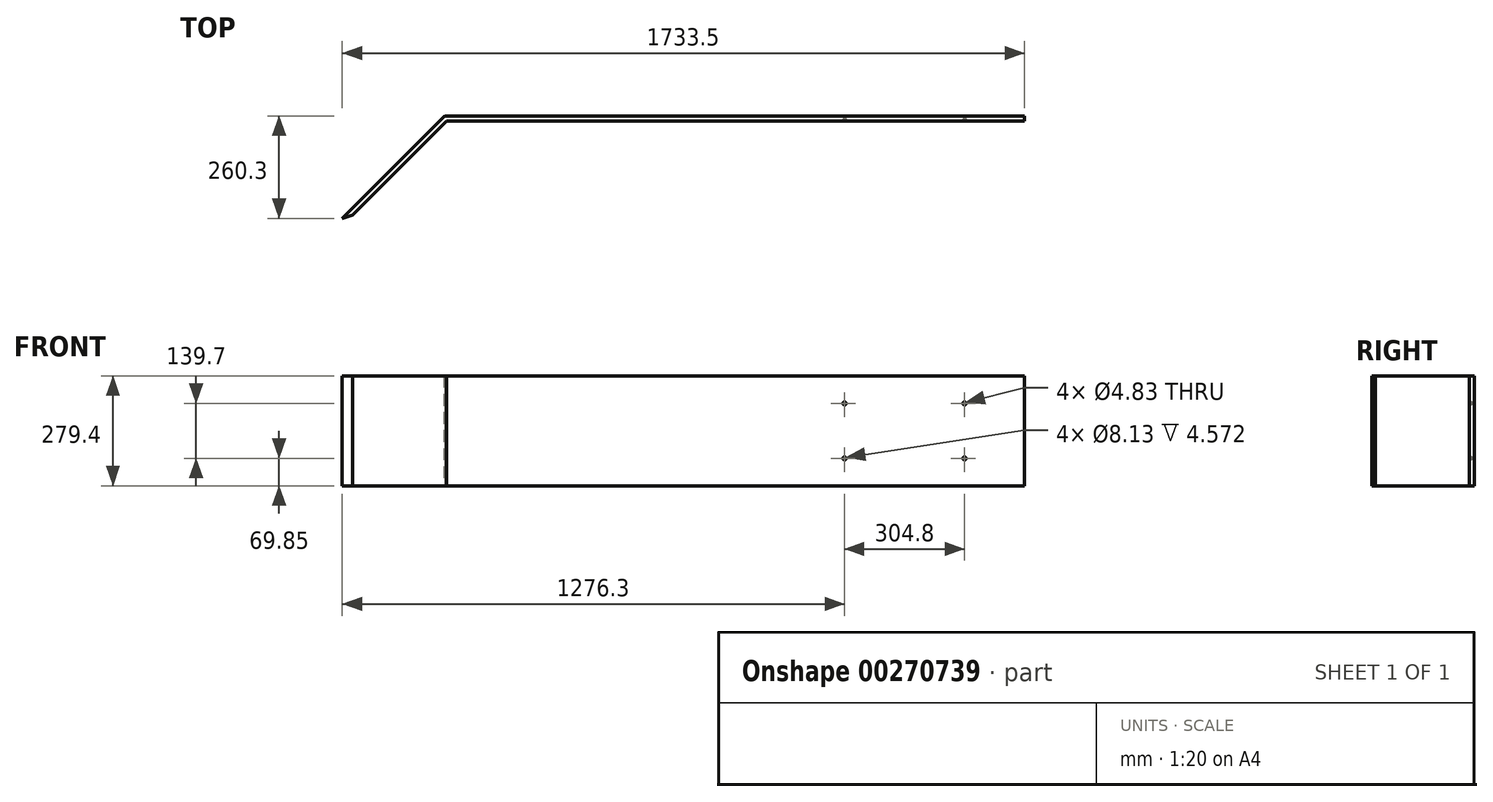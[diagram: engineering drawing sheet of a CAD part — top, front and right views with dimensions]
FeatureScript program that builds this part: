
annotation { "Feature Type Name" : "Feature", "Feature Type Description" : "" }
export const myFeature = defineFeature(function(context is Context, id is Id, definition is map)
    precondition{}
    {
        {
            var Q0;
            Q0=qCreatedBy(makeId("Front.planeOp"),FACE);
            var sketch = newSketch(context, id + "F0", { "sketchPlane" : qUnion([Q0])});
            skLineSegment(sketch, "E0.bottom", {"start": v(736.6, 139.7) * mm, "end": v(-736.6, 139.7) * mm});
            skLineSegment(sketch, "E0.top", {"start": v(736.6, -139.7) * mm, "end": v(-736.6, -139.7) * mm});
            skLineSegment(sketch, "E0.left", {"start": v(736.6, 139.7) * mm, "end": v(736.6, -139.7) * mm});
            skLineSegment(sketch, "E0.right", {"start": v(-736.6, 139.7) * mm, "end": v(-736.6, -139.7) * mm});
            skPoint(sketch, "E0.middle", {"position": v(0, 0) * mm});
            skSolve(sketch);
        }
        {
            var Q0;
            Q0 = qSketchRegion(id + "F0", true);
            extrude(context, id + "F1", {"entities" : qUnion([Q0]), "depth" : 12.7 * mm});
        }
        {
            var Q0;
            Q0=makeQuery(id+"F1.opExtrude","SWEPT_FACE",FACE,{"disambiguationData":[OSD([sQuery(id+"F0.wireOp",EDGE,"E0.bottom")])]});
            var sketch = newSketch(context, id + "F2", { "sketchPlane" : qUnion([Q0])});
            skLineSegment(sketch, "E1", {"start": v(-736.6, -12.7) * mm, "end": v(-736.6, 0) * mm});
            skLineSegment(sketch, "E2", {"start": v(-736.6, -12.7) * mm, "end": v(-731.34, -12.7) * mm});
            skLineSegment(sketch, "E3", {"start": v(-996.9, -260.3) * mm, "end": v(-736.6, 0) * mm});
            skLineSegment(sketch, "E4", {"start": v(-731.34, -12.7) * mm, "end": v(-969.96, -251.32) * mm});
            skLineSegment(sketch, "E5", {"start": v(-969.96, -251.32) * mm, "end": v(-996.9, -260.3) * mm});
            skSolve(sketch);
        }
        {
            var Q0;
            Q0 = qSketchRegion(id + "F2", true);
            extrude(context, id + "F3", {"entities" : qUnion([Q0]), "operationType" : NewBodyOperationType.ADD, "oppositeDirection" : true, "depth" : 279.4 * mm});
        }
        {
            var Q0;
            Q0=makeQuery(id+"F3.boolean.opBoolean","MERGE",EDGE,{"derivedFrom":[makeQuery(id+"F1.opExtrude","CAP_EDGE",EDGE,{"disambiguationData":[OSD([sQuery(id+"F0.wireOp",EDGE,"E0.right")])],"isStart":true}),makeQuery(id+"F3.opExtrude","SWEPT_EDGE",EDGE,{"disambiguationData":[OSD([sQuery(id+"F0.wireOp",EDGE,"E0.bottom"),sQuery(id+"F2.wireOp",EDGE,"E1"),sQuery(id+"F2.wireOp",EDGE,"E3")])]})]});
            var Q1;
            Q1=makeQuery(id+"F3.opExtrude","SWEPT_EDGE",EDGE,{"disambiguationData":[OSD([sQuery(id+"F0.wireOp",EDGE,"E0.bottom"),sQuery(id+"F2.wireOp",EDGE,"E2"),sQuery(id+"F2.wireOp",EDGE,"E4")])]});
            chamfer(context, id + "F4", {"entities" : qUnion([Q0, Q1]), "width" : 5.08 * mm, "tangentPropagation" : true});
        }
        {
            var Q0;
            Q0=makeQuery(id+"F1.opExtrude","CAP_FACE",FACE,{"disambiguationData":[OSD([sQuery(id+"F0.wireOp",EDGE,"E0.bottom"),sQuery(id+"F0.wireOp",EDGE,"E0.top"),sQuery(id+"F0.wireOp",EDGE,"E0.left"),sQuery(id+"F0.wireOp",EDGE,"E0.right")])],"isStart":false});
            var sketch = newSketch(context, id + "F5", { "sketchPlane" : qUnion([Q0])});
            skLineSegment(sketch, "E6", {"start": v(736.6, 139.7) * mm, "end": v(736.6, -139.7) * mm});
            skLineSegment(sketch, "E7", {"start": v(736.6, -139.7) * mm, "end": v(736.6, 0) * mm});
            skLineSegment(sketch, "E8", {"start": v(736.6, 0) * mm, "end": v(736.6, -69.85) * mm});
            skLineSegment(sketch, "E9", {"start": v(736.6, 0) * mm, "end": v(736.6, 139.7) * mm});
            skLineSegment(sketch, "E10", {"start": v(736.6, 69.85) * mm, "end": v(584.2, 69.85) * mm});
            skPoint(sketch, "E10.endSnap0", {"position": v(736.6, 69.85) * mm});
            skLineSegment(sketch, "E11", {"start": v(584.2, 69.85) * mm, "end": v(279.4, 69.85) * mm});
            skLineSegment(sketch, "E12", {"start": v(736.6, -69.85) * mm, "end": v(584.2, -69.85) * mm});
            skLineSegment(sketch, "E13", {"start": v(584.2, -69.85) * mm, "end": v(279.4, -69.85) * mm});
            skPoint(sketch, "E14", {"position": v(279.4, 69.85) * mm});
            skPoint(sketch, "E15", {"position": v(279.4, -69.85) * mm});
            skPoint(sketch, "E16", {"position": v(584.2, -69.85) * mm});
            skPoint(sketch, "E17", {"position": v(584.2, 69.85) * mm});
            skSolve(sketch);
        }
        {
            var Q0;
            Q0=sQuery(id+"F5.wireOp",VERTEX,"E14");
            var Q1;
            Q1=sQuery(id+"F5.wireOp",VERTEX,"E15");
            var Q2;
            Q2=sQuery(id+"F5.wireOp",VERTEX,"E16");
            var Q3;
            Q3=sQuery(id+"F5.wireOp",VERTEX,"E17");
            var Q4;
            Q4=makeQuery(id+"F1.opExtrude","SWEPT_BODY",BODY,{"disambiguationData":[OSD([sQuery(id+"F0.wireOp",EDGE,"E0.bottom"),sQuery(id+"F0.wireOp",EDGE,"E0.top"),sQuery(id+"F0.wireOp",EDGE,"E0.left"),sQuery(id+"F0.wireOp",EDGE,"E0.right")])]});
            hole(context, id + "F6", {"style" : HoleStyle.C_BORE, "endStyle" : HoleEndStyle.THROUGH, "holeDiameter" : 4.83 * mm, "cBoreDiameter" : 8.13 * mm, "cBoreDepth" : 4.57 * mm, "tappedDepth" : 12.7 * mm, "tapClearance" : 3, "locations" : qUnion([Q0, Q1, Q2, Q3]), "scope" : qUnion([Q4])});
        }
    });
